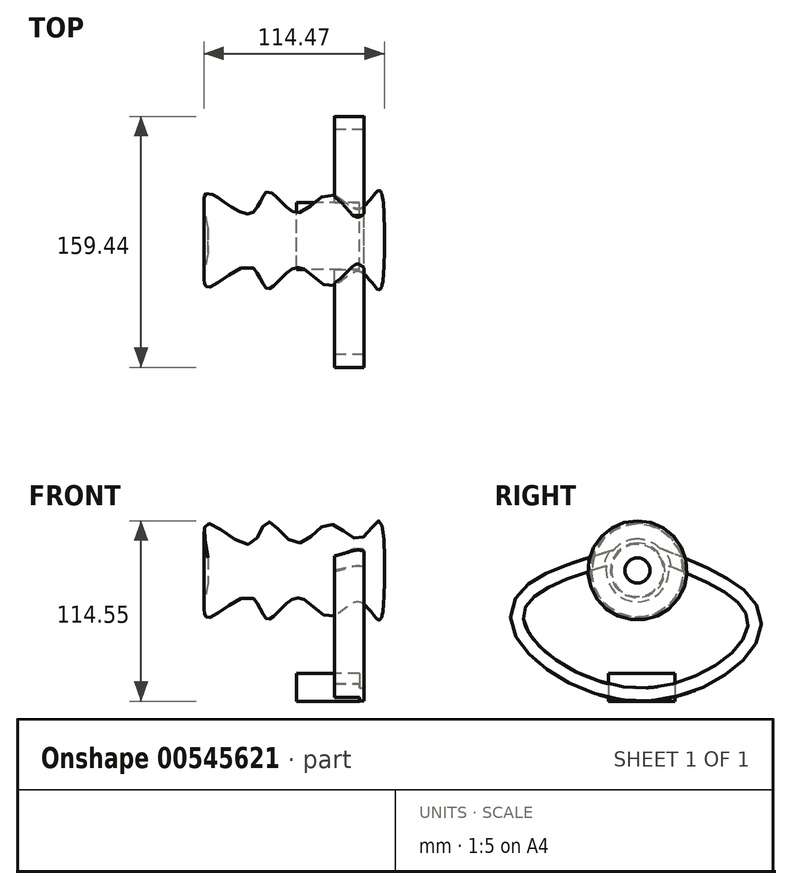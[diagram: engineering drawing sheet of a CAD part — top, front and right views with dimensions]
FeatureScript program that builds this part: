
annotation { "Feature Type Name" : "Feature", "Feature Type Description" : "" }
export const myFeature = defineFeature(function(context is Context, id is Id, definition is map)
    precondition{}
    {
        {
            var Q0;
            Q0=qCreatedBy(makeId("Front.planeOp"),FACE);
            var sketch = newSketch(context, id + "F0", { "sketchPlane" : qUnion([Q0])});
            skLineSegment(sketch, "E0", {"start": v(-56.17, 0) * mm, "end": v(55.73, 0) * mm});
            skLineSegment(sketch, "E1", {"start": v(55.73, 0) * mm, "end": v(55.73, 7.99) * mm});
            skLineSegment(sketch, "E2", {"start": v(-56.17, 0) * mm, "end": v(-56.17, 7.99) * mm});
            skFitSpline(sketch, "E3", {"points": [v(-56.17, 7.99) * mm, v(-56.17, 29.9) * mm, v(-29.3, 16.86) * mm, v(-18.34, 30.95) * mm, v(0, 17.38) * mm, v(20.8, 29.38) * mm, v(39.59, 19.99) * mm, v(52.1, 31.47) * mm, v(55.73, 7.99) * mm], "startDerivative": vector(-53.76, 264.7) * mm, "endDerivative": vector(5.92, -281.54) * mm});
            skSolve(sketch);
        }
        {
            var Q0;
            Q0=qCreatedBy(makeId("Front.planeOp"),FACE);
            var sketch = newSketch(context, id + "F1", { "sketchPlane" : qUnion([Q0])});
            skLineSegment(sketch, "E4.bottom", {"start": v(24, 13.57) * mm, "end": v(42.79, 13.57) * mm});
            skLineSegment(sketch, "E4.top", {"start": v(24, 5.22) * mm, "end": v(42.79, 5.22) * mm});
            skLineSegment(sketch, "E4.left", {"start": v(24, 13.57) * mm, "end": v(24, 5.22) * mm});
            skLineSegment(sketch, "E4.right", {"start": v(42.79, 13.57) * mm, "end": v(42.79, 5.22) * mm});
            skSolve(sketch);
        }
        {
            var Q0;
            Q0=qCreatedBy(makeId("Right.planeOp"),FACE);
            var sketch = newSketch(context, id + "F2", { "sketchPlane" : qUnion([Q0])});
            skLineSegment(sketch, "E5", {"start": v(0, 5.31) * mm, "end": v(-11.72, 5.31) * mm});
            skLineSegment(sketch, "E6", {"start": v(14.15, 5.31) * mm, "end": v(0, 5.31) * mm});
            skPoint(sketch, "E7.7.internal.orphan", {"position": v(14.15, 5.31) * mm});
            skFitSpline(sketch, "E8", {"points": [v(-11.72, 5.31) * mm, v(-72.52, -28.79) * mm, v(0, -74.7) * mm, v(70.4, -33.76) * mm, v(14.15, 5.31) * mm], "startDerivative": vector(-379.75, -112.05) * mm, "endDerivative": vector(-358.75, 143.43) * mm});
            skSolve(sketch);
        }
        {
            var Q0;
            Q0 = qSketchRegion(id + "F1", true);
            var Q1;
            Q1 = qConstructionFilter(qBodyType(qCreatedBy(id + "F2" ,EDGE), BodyType.WIRE), ConstructionObject.NO);
            sweep(context, id + "F3", {"profiles" : qUnion([Q0]), "path" : qUnion([Q1])});
        }
        {
            var Q0;
            Q0 = qSketchRegion(id + "F0", true);
            var Q1;
            Q1=sQuery(id+"F0.wireOp",EDGE,"E0");
            revolve(context, id + "F4", {"operationType" : NewBodyOperationType.ADD, "entities" : qUnion([Q0]), "axis" : qUnion([Q1]), "revolveType" : RevolveType.FULL});
        }
        {
            var Q0;
            Q0=qCreatedBy(makeId("Right.planeOp"),FACE);
            var sketch = newSketch(context, id + "F5", { "sketchPlane" : qUnion([Q0])});
            skLineSegment(sketch, "E9.bottom", {"start": v(-18.57, -65.38) * mm, "end": v(23.83, -65.38) * mm});
            skLineSegment(sketch, "E9.top", {"start": v(-18.57, -83.04) * mm, "end": v(23.83, -83.04) * mm});
            skLineSegment(sketch, "E9.left", {"start": v(-18.57, -65.38) * mm, "end": v(-18.57, -83.04) * mm});
            skLineSegment(sketch, "E9.right", {"start": v(23.83, -65.38) * mm, "end": v(23.83, -83.04) * mm});
            skSolve(sketch);
        }
        {
            var Q0;
            Q0 = qSketchRegion(id + "F5", true);
            extrude(context, id + "F6", {"entities" : qUnion([Q0]), "operationType" : NewBodyOperationType.ADD, "depth" : 40 * mm, "offsetDistance" : 25 * mm});
        }
    });
